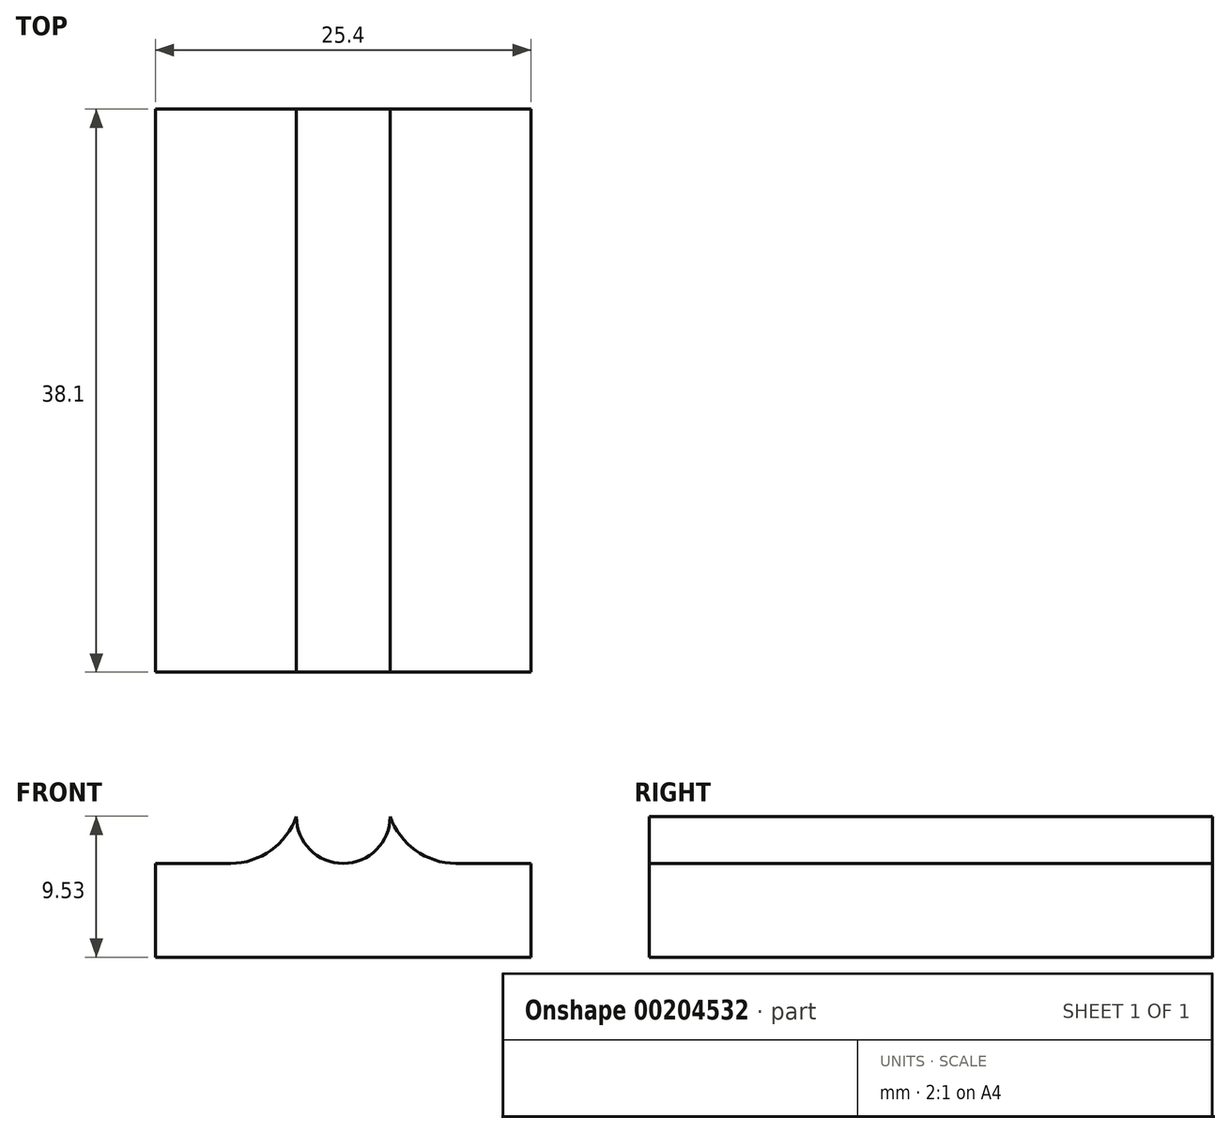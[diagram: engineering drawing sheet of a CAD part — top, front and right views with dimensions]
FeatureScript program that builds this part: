
annotation { "Feature Type Name" : "Feature", "Feature Type Description" : "" }
export const myFeature = defineFeature(function(context is Context, id is Id, definition is map)
    precondition{}
    {
        {
            var Q0;
            Q0=qCreatedBy(makeId("Front.planeOp"),FACE);
            var sketch = newSketch(context, id + "F0", { "sketchPlane" : qUnion([Q0])});
            skLineSegment(sketch, "E0", {"start": v(0, 0) * mm, "end": v(0, 6.35) * mm});
            skLineSegment(sketch, "E1", {"start": v(9.52, 6.35) * mm, "end": v(9.52, 9.53) * mm, "construction": true});
            skLineSegment(sketch, "E2", {"start": v(15.87, 9.53) * mm, "end": v(15.87, 6.35) * mm, "construction": true});
            skLineSegment(sketch, "E3", {"start": v(25.4, 6.35) * mm, "end": v(25.4, 0) * mm});
            skLineSegment(sketch, "E4", {"start": v(25.4, 0) * mm, "end": v(0, 0) * mm});
            skArc(sketch, "E5", {"start": v(9.52, 9.53) * mm, "mid": v(12.7, 6.35) * mm, "end": v(15.87, 9.53) * mm});
            skLineSegment(sketch, "E6", {"start": v(9.52, 6.35) * mm, "end": v(5.08, 6.35) * mm, "construction": true});
            skArc(sketch, "E7", {"start": v(5.08, 6.35) * mm, "mid": v(7.81, 7.23) * mm, "end": v(9.52, 9.53) * mm});
            skLineSegment(sketch, "E8", {"start": v(15.87, 6.35) * mm, "end": v(20.32, 6.35) * mm, "construction": true});
            skArc(sketch, "E9", {"start": v(15.87, 9.53) * mm, "mid": v(17.59, 7.23) * mm, "end": v(20.32, 6.35) * mm});
            skLineSegment(sketch, "E10", {"start": v(20.32, 6.35) * mm, "end": v(25.4, 6.35) * mm});
            skLineSegment(sketch, "E11", {"start": v(0, 6.35) * mm, "end": v(5.08, 6.35) * mm});
            skSolve(sketch);
        }
        {
            var Q0;
            Q0=makeQuery(id+"F0.imprint","IMPRINT",FACE,{"disambiguationData":[TD([[makeQuery(id+"F0.imprint","IMPRINT",EDGE,{"derivedFrom":sQuery(id+"F0.wireOp",EDGE,"E0")}),-1.0]])]});
            extrude(context, id + "F1", {"entities" : qUnion([Q0]), "depth" : 38.1 * mm});
        }
    });
